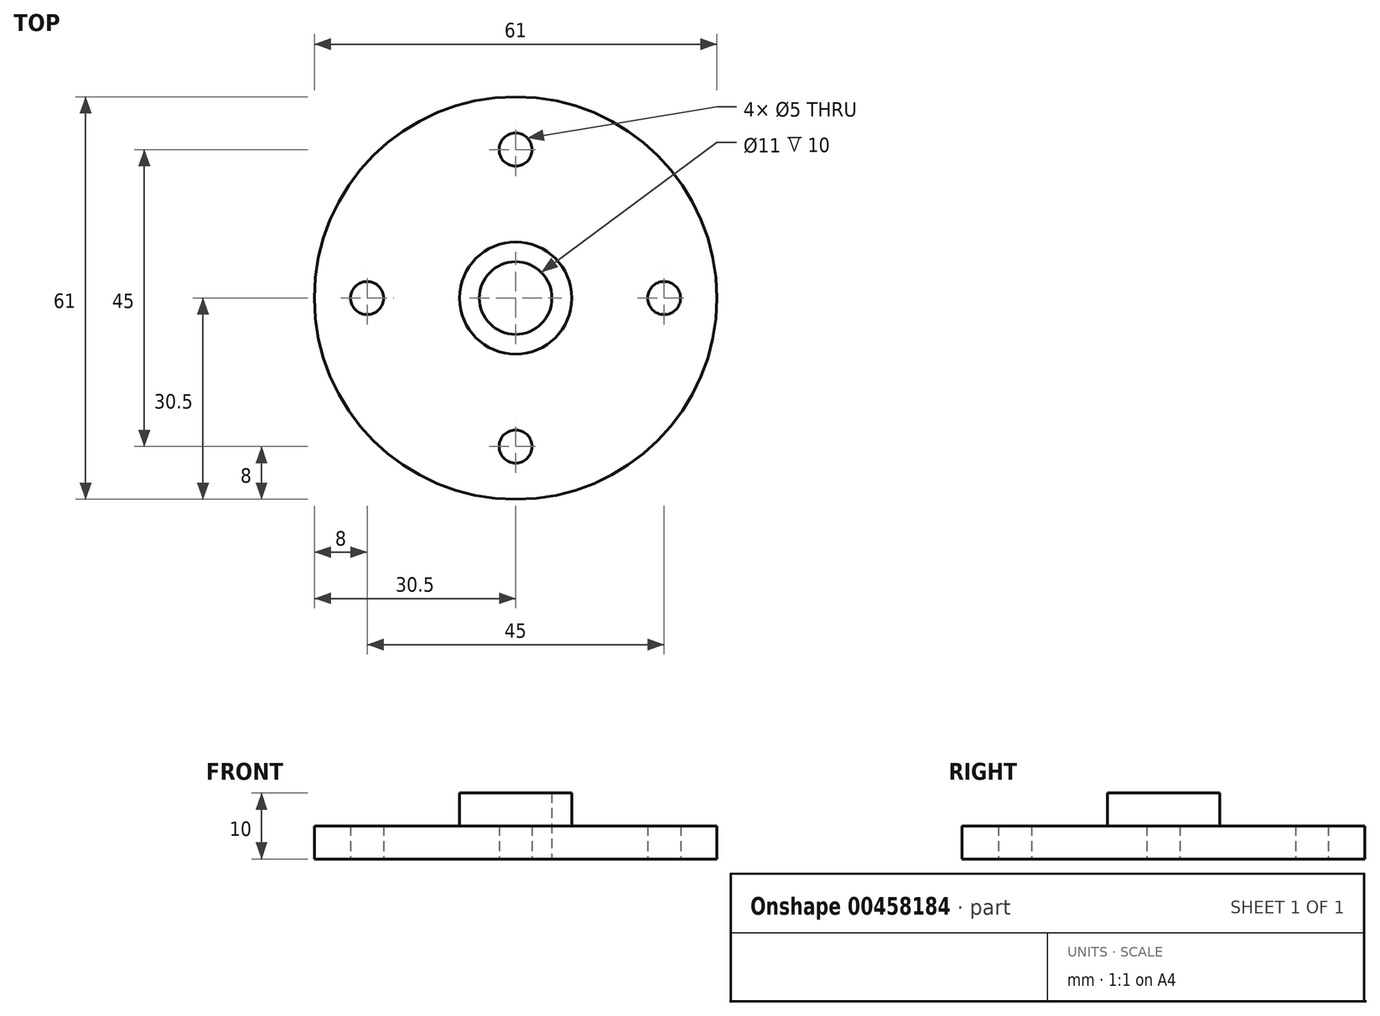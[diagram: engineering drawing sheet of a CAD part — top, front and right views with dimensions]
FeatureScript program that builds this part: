
annotation { "Feature Type Name" : "Feature", "Feature Type Description" : "" }
export const myFeature = defineFeature(function(context is Context, id is Id, definition is map)
    precondition{}
    {
        {
            var Q0;
            Q0=qCreatedBy(makeId("Top.planeOp"),FACE);
            var sketch = newSketch(context, id + "F0", { "sketchPlane" : qUnion([Q0])});
            skCircle(sketch, "E0", {"center": v(0, 0) * mm, "radius": 5.5 * mm});
            skCircle(sketch, "E1", {"center": v(0, 0) * mm, "radius": 25.5 * mm});
            skPoint(sketch, "E2", {"position": v(0, 22.5) * mm});
            skCircle(sketch, "E3", {"center": v(0, 0) * mm, "radius": 8.5 * mm});
            skPoint(sketch, "E4.1.0", {"position": v(-22.5, 0) * mm});
            skPoint(sketch, "E4.2.0", {"position": v(0, -22.5) * mm});
            skPoint(sketch, "E4.3.0", {"position": v(22.5, 0) * mm});
            skLineSegment(sketch, "E4.anchor1", {"start": v(0, 22.5) * mm, "end": v(0, 0) * mm, "construction": true});
            skLineSegment(sketch, "E4.anchor2", {"start": v(22.5, 0) * mm, "end": v(0, 0) * mm, "construction": true});
            skCircle(sketch, "E5", {"center": v(0, 0) * mm, "radius": 30.5 * mm});
            skSolve(sketch);
        }
        {
            var Q0;
            Q0=makeQuery(id+"F0.imprint","IMPRINT",FACE,{"disambiguationData":[TD([[makeQuery(id+"F0.imprint","IMPRINT",EDGE,{"derivedFrom":sQuery(id+"F0.wireOp",EDGE,"E1")}),1.0]])]});
            extrude(context, id + "F1", {"entities" : qUnion([Q0]), "depth" : 5 * mm});
        }
        {
            var Q0;
            Q0=makeQuery(id+"F0.imprint","IMPRINT",FACE,{"disambiguationData":[TD([[makeQuery(id+"F0.imprint","IMPRINT",EDGE,{"derivedFrom":sQuery(id+"F0.wireOp",EDGE,"E0")}),-1.0]])]});
            extrude(context, id + "F2", {"entities" : qUnion([Q0]), "operationType" : NewBodyOperationType.ADD, "depth" : 10 * mm});
        }
        {
            var Q0;
            Q0=sQuery(id+"F0.wireOp",VERTEX,"E4.1.0");
            var Q1;
            Q1=sQuery(id+"F0.wireOp",VERTEX,"E2");
            var Q2;
            Q2=sQuery(id+"F0.wireOp",VERTEX,"E4.5.0");
            var Q3;
            Q3=sQuery(id+"F0.wireOp",VERTEX,"E4.4.0");
            var Q4;
            Q4=sQuery(id+"F0.wireOp",VERTEX,"E4.3.0");
            var Q5;
            Q5=sQuery(id+"F0.wireOp",VERTEX,"E4.2.0");
            var Q6;
            Q6=makeQuery(id+"F1.opExtrude","SWEPT_BODY",BODY,{"disambiguationData":[OSD([sQuery(id+"F0.wireOp",EDGE,"E1"),sQuery(id+"F0.wireOp",EDGE,"E3")])]});
            hole(context, id + "F3", {"style" : HoleStyle.SIMPLE, "endStyle" : HoleEndStyle.THROUGH, "oppositeDirection" : true, "holeDiameter" : 5 * mm, "tappedDepth" : 12 * mm, "tapClearance" : 3, "locations" : qUnion([Q0, Q1, Q2, Q3, Q4, Q5]), "scope" : qUnion([Q6])});
        }
        {
            var Q0;
            Q0=makeQuery(id+"F0.imprint","IMPRINT",FACE,{"disambiguationData":[TD([[makeQuery(id+"F0.imprint","IMPRINT",EDGE,{"derivedFrom":sQuery(id+"F0.wireOp",EDGE,"E1")}),-1.0]])]});
            var Q1;
            Q1=makeQuery(id+"F1.opExtrude","CAP_FACE",FACE,{"disambiguationData":[OSD([sQuery(id+"F0.wireOp",EDGE,"E1"),sQuery(id+"F0.wireOp",EDGE,"E3")])],"isStart":false});
            extrude(context, id + "F4", {"entities" : qUnion([Q0]), "operationType" : NewBodyOperationType.ADD, "endBound" : BoundingType.UP_TO_SURFACE, "depth" : 25 * mm, "endBoundEntityFace" : qUnion([Q1]), "offsetDistance" : 25 * mm});
        }
    });
